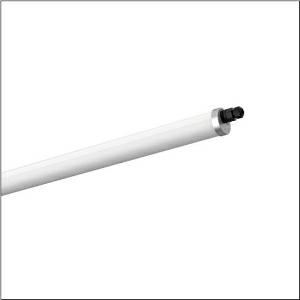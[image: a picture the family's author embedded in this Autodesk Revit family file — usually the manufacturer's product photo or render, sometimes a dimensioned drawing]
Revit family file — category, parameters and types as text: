
# Revit family: monsun_r__31_tube_51ft10dn4a0a_ff33
name_source: partatom
category: Lighting Fixtures
units: mm (PartAtom-declared; Revit-internal decimal feet)

## family parameters
Cut with Voids When Loaded = No
Host = Face
Light Source = No
Part Type = Normal
Room Calculation Point = No
Round Connector Dimension = Use Diameter
Shared = No

## types (1)
- Monsun® 31 Tube (1 x LED, 10000 lm, 58 W, 4000K)
    Apparent Load = 58 VA
    CIE Flux Codes = 42 71 90 91 100
    Color Rendering = 80
    Color Temperature = 4000K
    Default Elevation = 1800 mm
    Description = Monsun® 31 Tube, tubular luminaire, primary optical cover: diffuser, of PMMA, light emission: direct distribution, primary light characteristic: symmetric, installation type: suspended mounting, surface-mounted, LED, rated luminous flux: 10.000lm, luminous efficacy: 160lm/W, light colour: 840, colour temperature: 4000K, with with 1 terminal, 5-pole, max. 2.5mm², through-wiring: 5x 1.5mm², mains connection: 220..240V, AC, 50/60Hz, rated input power: 62W, housing, cylindrical, of PMMA, semi-transparent, matt white, length: 1.570mm, diameter: 75mm, end cap, of stainless steel (V2A), protection rating (complete): IP67/IP69K, insulation class (complete): insulation class I (protective earthing), certification: CE, UKCA, impact resistance: IK07, permissible operating ambient temperature: -20..+40°C, corresponds to IFS (International Featured Standards) requirements for safety and quality in the food industry, packaging unit: 1 piece
    Height = 83 mm
    Lamp = 1 x LED
    Lamp Light Flux = 10000 lm
    Lamp Power = 58 W
    Lamp count = 1
    Length = 1570 mm
    Luminous efficacy = 172 lm/W
    Manufacturer = Siteco
    ModVariant = No
    Model = 51FT10DN4A0A
    Mounting Place = Ceiling
    Mounting Type = Pendant
    Number of Poles = 1
    OnlyDefault = Yes
    Power Factor = 1
    Product Name = Monsun® 31 Tube
    Product group = tubular luminaire
    ProductGroupID = 907
    Protection Class = Protection class I
    RLX_Detail_Level = 1
    RlxData = <blob elided: 24909 chars, md5=831b6038>
    Socket = socket
    Standby Power = 0 W
    System Light Flux = 10000 lm
    System Power = 58 W
    Type Comments = Product without accessories
    Type Image = l_1228461.jpg
    URL = http://relux.com
    VarID = ---
    Voltage = 0 V
    Weight = 0.00 kg
    Width = 75 mm

## geometry (parser evidence)
native form markers: Blend x4, Sweep x13
no freeform markers — native parametric forms only
